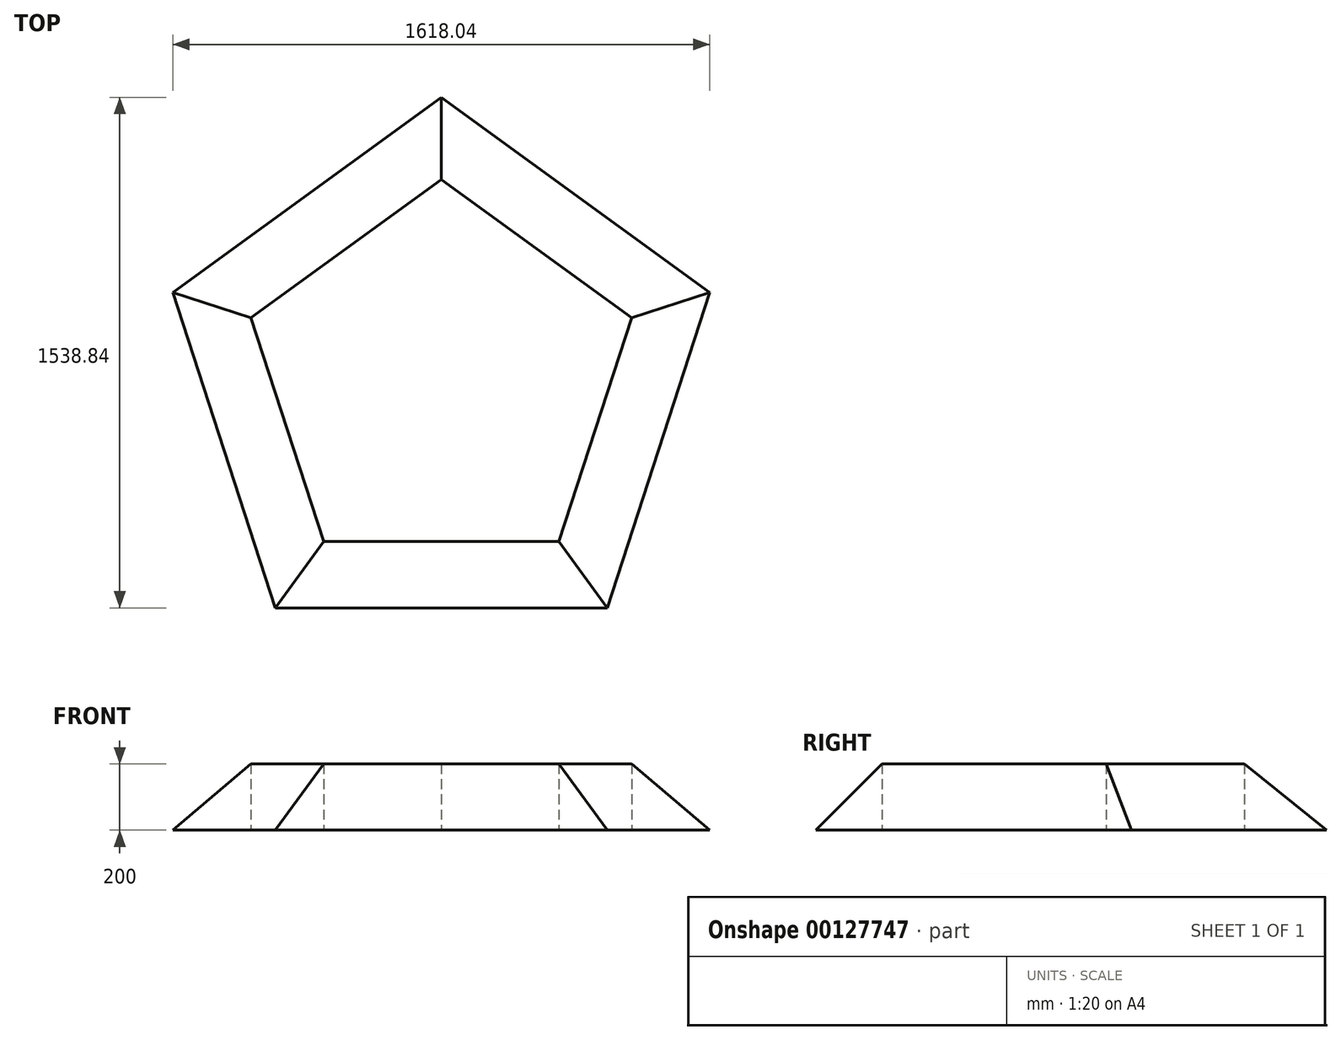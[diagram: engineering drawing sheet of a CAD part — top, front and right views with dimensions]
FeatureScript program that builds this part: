
annotation { "Feature Type Name" : "Feature", "Feature Type Description" : "" }
export const myFeature = defineFeature(function(context is Context, id is Id, definition is map)
    precondition{}
    {
        {
            var Q0;
            Q0=qCreatedBy(makeId("Top.planeOp"),FACE);
            var sketch = newSketch(context, id + "F0", { "sketchPlane" : qUnion([Q0])});
            skCircle(sketch, "E0.cCircle", {"center": v(0, 0) * mm, "radius": 850.65 * mm, "construction": true});
            skLineSegment(sketch, "E0.0", {"start": v(500, -688.2) * mm, "end": v(-500, -688.2) * mm});
            skLineSegment(sketch, "E0.1", {"start": v(-500, -688.2) * mm, "end": v(-809.02, 262.87) * mm});
            skLineSegment(sketch, "E0.2", {"start": v(-809.02, 262.87) * mm, "end": v(0, 850.65) * mm});
            skLineSegment(sketch, "E0.3", {"start": v(0, 850.65) * mm, "end": v(809.02, 262.87) * mm});
            skLineSegment(sketch, "E0.4", {"start": v(809.02, 262.87) * mm, "end": v(500, -688.2) * mm});
            skLineSegment(sketch, "E1.0", {"start": v(0, 603.44) * mm, "end": v(573.9, 186.47) * mm});
            skLineSegment(sketch, "E1.1", {"start": v(-573.9, 186.47) * mm, "end": v(0, 603.44) * mm});
            skLineSegment(sketch, "E1.2", {"start": v(573.9, 186.47) * mm, "end": v(354.7, -488.2) * mm});
            skLineSegment(sketch, "E1.3", {"start": v(354.7, -488.2) * mm, "end": v(-354.7, -488.2) * mm});
            skLineSegment(sketch, "E1.4", {"start": v(-354.7, -488.2) * mm, "end": v(-573.9, 186.47) * mm});
            skSolve(sketch);
        }
        {
            var Q0;
            Q0=sQuery(id+"F0.wireOp",EDGE,"E0.2");
            var Q1;
            Q1=sQuery(id+"F0.wireOp",EDGE,"E0.3");
            var Q2;
            Q2=sQuery(id+"F0.wireOp",EDGE,"E1.0");
            var Q3;
            Q3=sQuery(id+"F0.wireOp",EDGE,"E1.1");
            var Q4;
            Q4=sQuery(id+"F0.wireOp",EDGE,"E1.4");
            var Q5;
            Q5=sQuery(id+"F0.wireOp",EDGE,"E0.0");
            var Q6;
            Q6=sQuery(id+"F0.wireOp",EDGE,"E1.2");
            var Q7;
            Q7=sQuery(id+"F0.wireOp",EDGE,"E0.4");
            var Q8;
            Q8=sQuery(id+"F0.wireOp",EDGE,"E1.3");
            var Q9;
            Q9=sQuery(id+"F0.wireOp",EDGE,"E0.1");
            extrude(context, id + "F1", {"bodyType" : ToolBodyType.SURFACE, "surfaceEntities" : qUnion([Q0, Q1, Q2, Q3, Q4, Q5, Q6, Q7, Q8, Q9]), "depth" : 25 * mm});
        }
        {
            var Q0;
            Q0=makeQuery(id+"F0.imprint","IMPRINT",FACE,{"disambiguationData":[TD([[makeQuery(id+"F0.imprint","IMPRINT",EDGE,{"derivedFrom":sQuery(id+"F0.wireOp",EDGE,"E0.0")}),-1.0]])]});
            extrude(context, id + "F2", {"entities" : qUnion([Q0]), "depth" : 200 * mm});
        }
        {
            var Q0;
            Q0=makeQuery(id+"F2.opExtrude","CAP_EDGE",EDGE,{"disambiguationData":[OSD([sQuery(id+"F0.wireOp",EDGE,"E0.2")])],"isStart":false});
            var Q1;
            Q1=makeQuery(id+"F2.opExtrude","CAP_EDGE",EDGE,{"disambiguationData":[OSD([sQuery(id+"F0.wireOp",EDGE,"E0.3")])],"isStart":false});
            var Q2;
            Q2=makeQuery(id+"F2.opExtrude","CAP_EDGE",EDGE,{"disambiguationData":[OSD([sQuery(id+"F0.wireOp",EDGE,"E0.4")])],"isStart":false});
            var Q3;
            Q3=makeQuery(id+"F2.opExtrude","CAP_EDGE",EDGE,{"disambiguationData":[OSD([sQuery(id+"F0.wireOp",EDGE,"E0.0")])],"isStart":false});
            var Q4;
            Q4=makeQuery(id+"F2.opExtrude","CAP_EDGE",EDGE,{"disambiguationData":[OSD([sQuery(id+"F0.wireOp",EDGE,"E0.1")])],"isStart":false});
            chamfer(context, id + "F3", {"entities" : qUnion([Q0, Q1, Q2, Q3, Q4]), "width" : 200 * mm, "tangentPropagation" : true});
        }
    });
